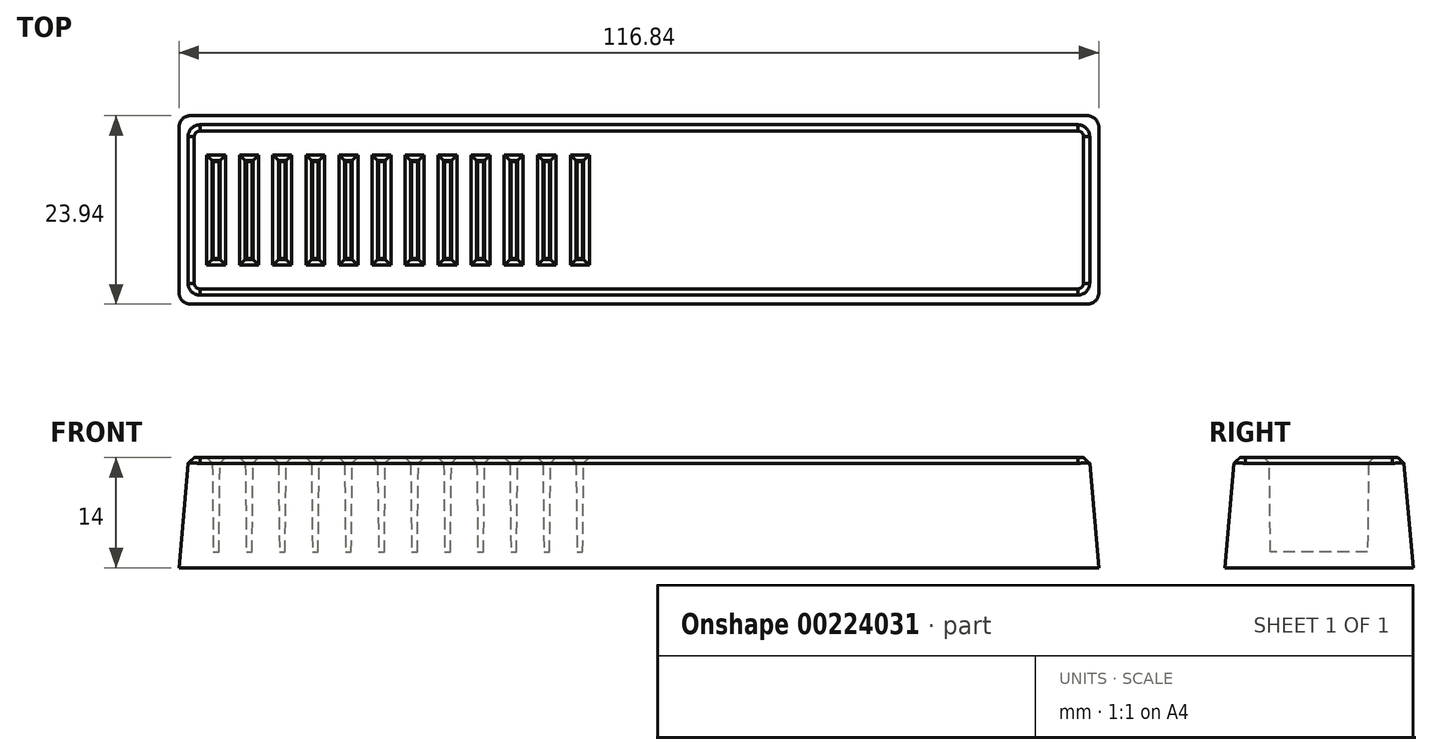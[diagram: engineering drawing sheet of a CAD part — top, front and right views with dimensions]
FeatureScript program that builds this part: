
annotation { "Feature Type Name" : "Feature", "Feature Type Description" : "" }
export const myFeature = defineFeature(function(context is Context, id is Id, definition is map)
    precondition{}
    {
        {
            var Q0;
            Q0=qCreatedBy(makeId("Top.planeOp"),FACE);
            var sketch = newSketch(context, id + "F0", { "sketchPlane" : qUnion([Q0])});
            skLineSegment(sketch, "E0.bottom", {"start": v(0, -10.75) * mm, "end": v(114.4, -10.75) * mm});
            skLineSegment(sketch, "E0.top", {"start": v(0, 10.75) * mm, "end": v(114.4, 10.75) * mm});
            skLineSegment(sketch, "E0.left", {"start": v(0, -10.75) * mm, "end": v(0, 10.75) * mm});
            skLineSegment(sketch, "E0.right", {"start": v(114.4, -10.75) * mm, "end": v(114.4, 10.75) * mm});
            skSolve(sketch);
        }
        {
            var Q0;
            Q0=makeQuery(id+"F0.imprint","IMPRINT",FACE,{"disambiguationData":[TD([[makeQuery(id+"F0.imprint","IMPRINT",EDGE,{"derivedFrom":sQuery(id+"F0.wireOp",EDGE,"E0.bottom")}),1.0]])]});
            var Q1;
            Q1=makeQuery(id+"F0.imprint","IMPRINT",FACE,{"disambiguationData":[TD([[makeQuery(id+"F0.imprint","IMPRINT",EDGE,{"derivedFrom":sQuery(id+"F0.wireOp",EDGE,"ueTfWKIi-SonA-VaYY-VuOx-WjBz5XcDr7Vq.bottom")}),1.0]])]});
            var Q2;
            Q2=makeQuery(id+"F0.imprint","IMPRINT",FACE,{"disambiguationData":[TD([[makeQuery(id+"F0.imprint","IMPRINT",EDGE,{"derivedFrom":sQuery(id+"F0.wireOp",EDGE,"e3a0679b-dacb-468f-a4c3-14299da426ac.1.0.0")}),-1.0]])]});
            var Q3;
            Q3=makeQuery(id+"F0.imprint","IMPRINT",FACE,{"disambiguationData":[TD([[makeQuery(id+"F0.imprint","IMPRINT",EDGE,{"derivedFrom":sQuery(id+"F0.wireOp",EDGE,"e3a0679b-dacb-468f-a4c3-14299da426ac.2.0.0")}),-1.0]])]});
            var Q4;
            Q4=makeQuery(id+"F0.imprint","IMPRINT",FACE,{"disambiguationData":[TD([[makeQuery(id+"F0.imprint","IMPRINT",EDGE,{"derivedFrom":sQuery(id+"F0.wireOp",EDGE,"5b3f68b4-6977-4b90-b81e-3b0594952896.0.3.0")}),-1.0]])]});
            var Q5;
            Q5=makeQuery(id+"F0.imprint","IMPRINT",FACE,{"disambiguationData":[TD([[makeQuery(id+"F0.imprint","IMPRINT",EDGE,{"derivedFrom":sQuery(id+"F0.wireOp",EDGE,"5b3f68b4-6977-4b90-b81e-3b0594952896.0.4.0")}),-1.0]])]});
            var Q6;
            Q6=makeQuery(id+"F0.imprint","IMPRINT",FACE,{"disambiguationData":[TD([[makeQuery(id+"F0.imprint","IMPRINT",EDGE,{"derivedFrom":sQuery(id+"F0.wireOp",EDGE,"5b3f68b4-6977-4b90-b81e-3b0594952896.0.6.0")}),-1.0]])]});
            var Q7;
            Q7=makeQuery(id+"F0.imprint","IMPRINT",FACE,{"disambiguationData":[TD([[makeQuery(id+"F0.imprint","IMPRINT",EDGE,{"derivedFrom":sQuery(id+"F0.wireOp",EDGE,"5b3f68b4-6977-4b90-b81e-3b0594952896.0.7.0")}),-1.0]])]});
            var Q8;
            Q8=makeQuery(id+"F0.imprint","IMPRINT",FACE,{"disambiguationData":[TD([[makeQuery(id+"F0.imprint","IMPRINT",EDGE,{"derivedFrom":sQuery(id+"F0.wireOp",EDGE,"5b3f68b4-6977-4b90-b81e-3b0594952896.0.5.0")}),-1.0]])]});
            var Q9;
            Q9=makeQuery(id+"F0.imprint","IMPRINT",FACE,{"disambiguationData":[TD([[makeQuery(id+"F0.imprint","IMPRINT",EDGE,{"derivedFrom":sQuery(id+"F0.wireOp",EDGE,"7b803989-21a2-4f2c-bcc4-6ed27433c35e.0.8.0")}),-1.0]])]});
            var Q10;
            Q10=makeQuery(id+"F0.imprint","IMPRINT",FACE,{"disambiguationData":[TD([[makeQuery(id+"F0.imprint","IMPRINT",EDGE,{"derivedFrom":sQuery(id+"F0.wireOp",EDGE,"7b803989-21a2-4f2c-bcc4-6ed27433c35e.0.9.0")}),-1.0]])]});
            var Q11;
            Q11=makeQuery(id+"F0.imprint","IMPRINT",FACE,{"disambiguationData":[TD([[makeQuery(id+"F0.imprint","IMPRINT",EDGE,{"derivedFrom":sQuery(id+"F0.wireOp",EDGE,"7b803989-21a2-4f2c-bcc4-6ed27433c35e.0.10.0")}),-1.0]])]});
            var Q12;
            Q12=makeQuery(id+"F0.imprint","IMPRINT",FACE,{"disambiguationData":[TD([[makeQuery(id+"F0.imprint","IMPRINT",EDGE,{"derivedFrom":sQuery(id+"F0.wireOp",EDGE,"7b803989-21a2-4f2c-bcc4-6ed27433c35e.0.11.0")}),-1.0]])]});
            extrude(context, id + "F1", {"entities" : qUnion([Q0, Q1, Q2, Q3, Q4, Q5, Q6, Q7, Q8, Q9, Q10, Q11, Q12]), "oppositeDirection" : true, "offsetDistance" : 25 * mm, "depth" : 14 * mm, "hasDraft" : true, "draftAngle" : 5 * degree});
        }
        {
            var Q0;
            Q0=makeQuery(id+"F1.opExtrude","CAP_FACE",FACE,{"disambiguationData":[OSD([sQuery(id+"F0.wireOp",EDGE,"E0.bottom"),sQuery(id+"F0.wireOp",EDGE,"E0.top"),sQuery(id+"F0.wireOp",EDGE,"E0.left"),sQuery(id+"F0.wireOp",EDGE,"E0.right"),sQuery(id+"F0.wireOp",EDGE,"xGjfcOIm-HSnc-pNGx-gc4Z-AyiedxzzNEQQ"),sQuery(id+"F0.wireOp",EDGE,"YTJknqgt-HmQx-HAe6-ae00-YsNhZU43DuuP"),sQuery(id+"F0.wireOp",EDGE,"M8XJMNeE-EDg2-ARwt-BN1e-G1xgn0dm087A"),sQuery(id+"F0.wireOp",EDGE,"pM8agkuu-0SVb-TDAc-swg6-VZ6Kp682kka8"),sQuery(id+"F0.wireOp",EDGE,"8114b382-a146-4457-b184-7c86869df042.filletArc"),sQuery(id+"F0.wireOp",EDGE,"38438068-d717-4d8c-9960-bff2e024779f.filletArc"),sQuery(id+"F0.wireOp",EDGE,"4a753ca2-9ca1-48ae-85e5-495222f0e263.filletArc"),sQuery(id+"F0.wireOp",EDGE,"6b48d99f-0b37-43ed-b982-f66e7705704f.filletArc")])],"isStart":true});
            var sketch = newSketch(context, id + "F2", { "sketchPlane" : qUnion([Q0])});
            skLineSegment(sketch, "E1.bottom", {"start": v(4, 6.3) * mm, "end": v(3, 6.3) * mm, "construction": true});
            skLineSegment(sketch, "E1.top", {"start": v(4, -6.3) * mm, "end": v(3, -6.3) * mm, "construction": true});
            skLineSegment(sketch, "E1.left", {"start": v(4, 6.3) * mm, "end": v(4, -6.3) * mm, "construction": true});
            skLineSegment(sketch, "E1.right", {"start": v(3, 6.3) * mm, "end": v(3, -6.3) * mm, "construction": true});
            skPoint(sketch, "E1.middle", {"position": v(3.5, 0) * mm});
            skLineSegment(sketch, "E2", {"start": v(3, 6.3) * mm, "end": v(3, -6.3) * mm});
            skLineSegment(sketch, "E3", {"start": v(4, -6.3) * mm, "end": v(4, 6.3) * mm});
            skLineSegment(sketch, "E4", {"start": v(3, -6.3) * mm, "end": v(4, -6.3) * mm});
            skLineSegment(sketch, "E5", {"start": v(3, 6.3) * mm, "end": v(4, 6.3) * mm});
            skLineSegment(sketch, "E6.0.1.0", {"start": v(8.2, -6.3) * mm, "end": v(7.2, -6.3) * mm, "construction": true});
            skLineSegment(sketch, "E6.1.1.0", {"start": v(8.2, 6.3) * mm, "end": v(8.2, -6.3) * mm, "construction": true});
            skLineSegment(sketch, "E6.2.1.0", {"start": v(7.2, 6.3) * mm, "end": v(7.2, -6.3) * mm, "construction": true});
            skLineSegment(sketch, "E6.3.1.0", {"start": v(8.2, 6.3) * mm, "end": v(7.2, 6.3) * mm, "construction": true});
            skPoint(sketch, "E6.4.1.0", {"position": v(7.7, 0) * mm});
            skLineSegment(sketch, "E6.5.1.0", {"start": v(7.2, -6.3) * mm, "end": v(8.2, -6.3) * mm});
            skPoint(sketch, "E6.6.1.0", {"position": v(7.7, 0) * mm});
            skLineSegment(sketch, "E6.7.1.0", {"start": v(7.2, 6.3) * mm, "end": v(7.2, -6.3) * mm});
            skLineSegment(sketch, "E6.8.1.0", {"start": v(8.2, -6.3) * mm, "end": v(8.2, 6.3) * mm});
            skLineSegment(sketch, "E6.9.1.0", {"start": v(7.2, 6.3) * mm, "end": v(8.2, 6.3) * mm});
            skLineSegment(sketch, "E6.0.2.0", {"start": v(12.4, -6.3) * mm, "end": v(11.4, -6.3) * mm, "construction": true});
            skLineSegment(sketch, "E6.1.2.0", {"start": v(12.4, 6.3) * mm, "end": v(12.4, -6.3) * mm, "construction": true});
            skLineSegment(sketch, "E6.2.2.0", {"start": v(11.4, 6.3) * mm, "end": v(11.4, -6.3) * mm, "construction": true});
            skLineSegment(sketch, "E6.3.2.0", {"start": v(12.4, 6.3) * mm, "end": v(11.4, 6.3) * mm, "construction": true});
            skPoint(sketch, "E6.4.2.0", {"position": v(11.9, 0) * mm});
            skLineSegment(sketch, "E6.5.2.0", {"start": v(11.4, -6.3) * mm, "end": v(12.4, -6.3) * mm});
            skPoint(sketch, "E6.6.2.0", {"position": v(11.9, 0) * mm});
            skLineSegment(sketch, "E6.7.2.0", {"start": v(11.4, 6.3) * mm, "end": v(11.4, -6.3) * mm});
            skLineSegment(sketch, "E6.8.2.0", {"start": v(12.4, -6.3) * mm, "end": v(12.4, 6.3) * mm});
            skLineSegment(sketch, "E6.9.2.0", {"start": v(11.4, 6.3) * mm, "end": v(12.4, 6.3) * mm});
            skLineSegment(sketch, "E6.0.3.0", {"start": v(16.6, -6.3) * mm, "end": v(15.6, -6.3) * mm, "construction": true});
            skLineSegment(sketch, "E6.1.3.0", {"start": v(16.6, 6.3) * mm, "end": v(16.6, -6.3) * mm, "construction": true});
            skLineSegment(sketch, "E6.2.3.0", {"start": v(15.6, 6.3) * mm, "end": v(15.6, -6.3) * mm, "construction": true});
            skLineSegment(sketch, "E6.3.3.0", {"start": v(16.6, 6.3) * mm, "end": v(15.6, 6.3) * mm, "construction": true});
            skPoint(sketch, "E6.4.3.0", {"position": v(16.1, 0) * mm});
            skLineSegment(sketch, "E6.5.3.0", {"start": v(15.6, -6.3) * mm, "end": v(16.6, -6.3) * mm});
            skPoint(sketch, "E6.6.3.0", {"position": v(16.1, 0) * mm});
            skLineSegment(sketch, "E6.7.3.0", {"start": v(15.6, 6.3) * mm, "end": v(15.6, -6.3) * mm});
            skLineSegment(sketch, "E6.8.3.0", {"start": v(16.6, -6.3) * mm, "end": v(16.6, 6.3) * mm});
            skLineSegment(sketch, "E6.9.3.0", {"start": v(15.6, 6.3) * mm, "end": v(16.6, 6.3) * mm});
            skLineSegment(sketch, "E6.0.4.0", {"start": v(20.8, -6.3) * mm, "end": v(19.8, -6.3) * mm, "construction": true});
            skLineSegment(sketch, "E6.1.4.0", {"start": v(20.8, 6.3) * mm, "end": v(20.8, -6.3) * mm, "construction": true});
            skLineSegment(sketch, "E6.2.4.0", {"start": v(19.8, 6.3) * mm, "end": v(19.8, -6.3) * mm, "construction": true});
            skLineSegment(sketch, "E6.3.4.0", {"start": v(20.8, 6.3) * mm, "end": v(19.8, 6.3) * mm, "construction": true});
            skPoint(sketch, "E6.4.4.0", {"position": v(20.3, 0) * mm});
            skLineSegment(sketch, "E6.5.4.0", {"start": v(19.8, -6.3) * mm, "end": v(20.8, -6.3) * mm});
            skPoint(sketch, "E6.6.4.0", {"position": v(20.3, 0) * mm});
            skLineSegment(sketch, "E6.7.4.0", {"start": v(19.8, 6.3) * mm, "end": v(19.8, -6.3) * mm});
            skLineSegment(sketch, "E6.8.4.0", {"start": v(20.8, -6.3) * mm, "end": v(20.8, 6.3) * mm});
            skLineSegment(sketch, "E6.9.4.0", {"start": v(19.8, 6.3) * mm, "end": v(20.8, 6.3) * mm});
            skLineSegment(sketch, "E6.0.5.0", {"start": v(25, -6.3) * mm, "end": v(24, -6.3) * mm, "construction": true});
            skLineSegment(sketch, "E6.1.5.0", {"start": v(25, 6.3) * mm, "end": v(25, -6.3) * mm, "construction": true});
            skLineSegment(sketch, "E6.2.5.0", {"start": v(24, 6.3) * mm, "end": v(24, -6.3) * mm, "construction": true});
            skLineSegment(sketch, "E6.3.5.0", {"start": v(25, 6.3) * mm, "end": v(24, 6.3) * mm, "construction": true});
            skPoint(sketch, "E6.4.5.0", {"position": v(24.5, 0) * mm});
            skLineSegment(sketch, "E6.5.5.0", {"start": v(24, -6.3) * mm, "end": v(25, -6.3) * mm});
            skPoint(sketch, "E6.6.5.0", {"position": v(24.5, 0) * mm});
            skLineSegment(sketch, "E6.7.5.0", {"start": v(24, 6.3) * mm, "end": v(24, -6.3) * mm});
            skLineSegment(sketch, "E6.8.5.0", {"start": v(25, -6.3) * mm, "end": v(25, 6.3) * mm});
            skLineSegment(sketch, "E6.9.5.0", {"start": v(24, 6.3) * mm, "end": v(25, 6.3) * mm});
            skLineSegment(sketch, "E6.0.6.0", {"start": v(29.2, -6.3) * mm, "end": v(28.2, -6.3) * mm, "construction": true});
            skLineSegment(sketch, "E6.1.6.0", {"start": v(29.2, 6.3) * mm, "end": v(29.2, -6.3) * mm, "construction": true});
            skLineSegment(sketch, "E6.2.6.0", {"start": v(28.2, 6.3) * mm, "end": v(28.2, -6.3) * mm, "construction": true});
            skLineSegment(sketch, "E6.3.6.0", {"start": v(29.2, 6.3) * mm, "end": v(28.2, 6.3) * mm, "construction": true});
            skPoint(sketch, "E6.4.6.0", {"position": v(28.7, 0) * mm});
            skLineSegment(sketch, "E6.5.6.0", {"start": v(28.2, -6.3) * mm, "end": v(29.2, -6.3) * mm});
            skPoint(sketch, "E6.6.6.0", {"position": v(28.7, 0) * mm});
            skLineSegment(sketch, "E6.7.6.0", {"start": v(28.2, 6.3) * mm, "end": v(28.2, -6.3) * mm});
            skLineSegment(sketch, "E6.8.6.0", {"start": v(29.2, -6.3) * mm, "end": v(29.2, 6.3) * mm});
            skLineSegment(sketch, "E6.9.6.0", {"start": v(28.2, 6.3) * mm, "end": v(29.2, 6.3) * mm});
            skLineSegment(sketch, "E6.0.7.0", {"start": v(33.4, -6.3) * mm, "end": v(32.4, -6.3) * mm, "construction": true});
            skLineSegment(sketch, "E6.1.7.0", {"start": v(33.4, 6.3) * mm, "end": v(33.4, -6.3) * mm, "construction": true});
            skLineSegment(sketch, "E6.2.7.0", {"start": v(32.4, 6.3) * mm, "end": v(32.4, -6.3) * mm, "construction": true});
            skLineSegment(sketch, "E6.3.7.0", {"start": v(33.4, 6.3) * mm, "end": v(32.4, 6.3) * mm, "construction": true});
            skPoint(sketch, "E6.4.7.0", {"position": v(32.9, 0) * mm});
            skLineSegment(sketch, "E6.5.7.0", {"start": v(32.4, -6.3) * mm, "end": v(33.4, -6.3) * mm});
            skPoint(sketch, "E6.6.7.0", {"position": v(32.9, 0) * mm});
            skLineSegment(sketch, "E6.7.7.0", {"start": v(32.4, 6.3) * mm, "end": v(32.4, -6.3) * mm});
            skLineSegment(sketch, "E6.8.7.0", {"start": v(33.4, -6.3) * mm, "end": v(33.4, 6.3) * mm});
            skLineSegment(sketch, "E6.9.7.0", {"start": v(32.4, 6.3) * mm, "end": v(33.4, 6.3) * mm});
            skLineSegment(sketch, "E6.0.8.0", {"start": v(37.6, -6.3) * mm, "end": v(36.6, -6.3) * mm, "construction": true});
            skLineSegment(sketch, "E6.1.8.0", {"start": v(37.6, 6.3) * mm, "end": v(37.6, -6.3) * mm, "construction": true});
            skLineSegment(sketch, "E6.2.8.0", {"start": v(36.6, 6.3) * mm, "end": v(36.6, -6.3) * mm, "construction": true});
            skLineSegment(sketch, "E6.3.8.0", {"start": v(37.6, 6.3) * mm, "end": v(36.6, 6.3) * mm, "construction": true});
            skPoint(sketch, "E6.4.8.0", {"position": v(37.1, 0) * mm});
            skLineSegment(sketch, "E6.5.8.0", {"start": v(36.6, -6.3) * mm, "end": v(37.6, -6.3) * mm});
            skPoint(sketch, "E6.6.8.0", {"position": v(37.1, 0) * mm});
            skLineSegment(sketch, "E6.7.8.0", {"start": v(36.6, 6.3) * mm, "end": v(36.6, -6.3) * mm});
            skLineSegment(sketch, "E6.8.8.0", {"start": v(37.6, -6.3) * mm, "end": v(37.6, 6.3) * mm});
            skLineSegment(sketch, "E6.9.8.0", {"start": v(36.6, 6.3) * mm, "end": v(37.6, 6.3) * mm});
            skLineSegment(sketch, "E6.0.9.0", {"start": v(41.8, -6.3) * mm, "end": v(40.8, -6.3) * mm, "construction": true});
            skLineSegment(sketch, "E6.1.9.0", {"start": v(41.8, 6.3) * mm, "end": v(41.8, -6.3) * mm, "construction": true});
            skLineSegment(sketch, "E6.2.9.0", {"start": v(40.8, 6.3) * mm, "end": v(40.8, -6.3) * mm, "construction": true});
            skLineSegment(sketch, "E6.3.9.0", {"start": v(41.8, 6.3) * mm, "end": v(40.8, 6.3) * mm, "construction": true});
            skPoint(sketch, "E6.4.9.0", {"position": v(41.3, 0) * mm});
            skLineSegment(sketch, "E6.5.9.0", {"start": v(40.8, -6.3) * mm, "end": v(41.8, -6.3) * mm});
            skPoint(sketch, "E6.6.9.0", {"position": v(41.3, 0) * mm});
            skLineSegment(sketch, "E6.7.9.0", {"start": v(40.8, 6.3) * mm, "end": v(40.8, -6.3) * mm});
            skLineSegment(sketch, "E6.8.9.0", {"start": v(41.8, -6.3) * mm, "end": v(41.8, 6.3) * mm});
            skLineSegment(sketch, "E6.9.9.0", {"start": v(40.8, 6.3) * mm, "end": v(41.8, 6.3) * mm});
            skLineSegment(sketch, "E6.0.10.0", {"start": v(46, -6.3) * mm, "end": v(45, -6.3) * mm, "construction": true});
            skLineSegment(sketch, "E6.1.10.0", {"start": v(46, 6.3) * mm, "end": v(46, -6.3) * mm, "construction": true});
            skLineSegment(sketch, "E6.2.10.0", {"start": v(45, 6.3) * mm, "end": v(45, -6.3) * mm, "construction": true});
            skLineSegment(sketch, "E6.3.10.0", {"start": v(46, 6.3) * mm, "end": v(45, 6.3) * mm, "construction": true});
            skPoint(sketch, "E6.4.10.0", {"position": v(45.5, 0) * mm});
            skLineSegment(sketch, "E6.5.10.0", {"start": v(45, -6.3) * mm, "end": v(46, -6.3) * mm});
            skPoint(sketch, "E6.6.10.0", {"position": v(45.5, 0) * mm});
            skLineSegment(sketch, "E6.7.10.0", {"start": v(45, 6.3) * mm, "end": v(45, -6.3) * mm});
            skLineSegment(sketch, "E6.8.10.0", {"start": v(46, -6.3) * mm, "end": v(46, 6.3) * mm});
            skLineSegment(sketch, "E6.9.10.0", {"start": v(45, 6.3) * mm, "end": v(46, 6.3) * mm});
            skLineSegment(sketch, "E6.0.11.0", {"start": v(50.2, -6.3) * mm, "end": v(49.2, -6.3) * mm, "construction": true});
            skLineSegment(sketch, "E6.1.11.0", {"start": v(50.2, 6.3) * mm, "end": v(50.2, -6.3) * mm, "construction": true});
            skLineSegment(sketch, "E6.2.11.0", {"start": v(49.2, 6.3) * mm, "end": v(49.2, -6.3) * mm, "construction": true});
            skLineSegment(sketch, "E6.3.11.0", {"start": v(50.2, 6.3) * mm, "end": v(49.2, 6.3) * mm, "construction": true});
            skPoint(sketch, "E6.4.11.0", {"position": v(49.7, 0) * mm});
            skLineSegment(sketch, "E6.5.11.0", {"start": v(49.2, -6.3) * mm, "end": v(50.2, -6.3) * mm});
            skPoint(sketch, "E6.6.11.0", {"position": v(49.7, 0) * mm});
            skLineSegment(sketch, "E6.7.11.0", {"start": v(49.2, 6.3) * mm, "end": v(49.2, -6.3) * mm});
            skLineSegment(sketch, "E6.8.11.0", {"start": v(50.2, -6.3) * mm, "end": v(50.2, 6.3) * mm});
            skLineSegment(sketch, "E6.9.11.0", {"start": v(49.2, 6.3) * mm, "end": v(50.2, 6.3) * mm});
            skLineSegment(sketch, "E6.direction1", {"start": v(3, -6.3) * mm, "end": v(7.2, -6.3) * mm, "construction": true});
            skSolve(sketch);
        }
        {
            var Q0;
            Q0 = qSketchRegion(id + "F2", true);
            extrude(context, id + "F3", {"entities" : qUnion([Q0]), "operationType" : NewBodyOperationType.REMOVE, "oppositeDirection" : true, "offsetDistance" : 25 * mm, "depth" : 12 * mm, "hasDraft" : true, "draftAngle" : .66 * degree, "draftPullDirection" : true});
        }
        {
            var Q0;
            Q0=makeQuery(id+"F1.opExtrude","SWEPT_EDGE",EDGE,{"disambiguationData":[OSD([sQuery(id+"F0.wireOp",EDGE,"E0.bottom"),sQuery(id+"F0.wireOp",EDGE,"E0.left")])]});
            var Q1;
            Q1=makeQuery(id+"F1.opExtrude","SWEPT_EDGE",EDGE,{"disambiguationData":[OSD([sQuery(id+"F0.wireOp",EDGE,"E0.top"),sQuery(id+"F0.wireOp",EDGE,"E0.left")])]});
            var Q2;
            Q2=makeQuery(id+"F1.opExtrude","SWEPT_EDGE",EDGE,{"disambiguationData":[OSD([sQuery(id+"F0.wireOp",EDGE,"E0.top"),sQuery(id+"F0.wireOp",EDGE,"E0.right")])]});
            var Q3;
            Q3=makeQuery(id+"F1.opExtrude","SWEPT_EDGE",EDGE,{"disambiguationData":[OSD([sQuery(id+"F0.wireOp",EDGE,"E0.bottom"),sQuery(id+"F0.wireOp",EDGE,"E0.right")])]});
            fillet(context, id + "F4", {"entities" : qUnion([Q0, Q1, Q2, Q3]), "radius" : 1.5 * mm, "tangentPropagation" : true, "allowEdgeOverflow" : false});
        }
        {
            var Q0;
            Q0=makeQuery(id+"F1.opExtrude","CAP_FACE",FACE,{"disambiguationData":[OSD([sQuery(id+"F0.wireOp",EDGE,"E0.bottom"),sQuery(id+"F0.wireOp",EDGE,"E0.top"),sQuery(id+"F0.wireOp",EDGE,"E0.left"),sQuery(id+"F0.wireOp",EDGE,"E0.right")])],"isStart":true});
            chamfer(context, id + "F5", {"entities" : qUnion([Q0]), "width" : .7 * mm, "tangentPropagation" : true});
        }
    });
